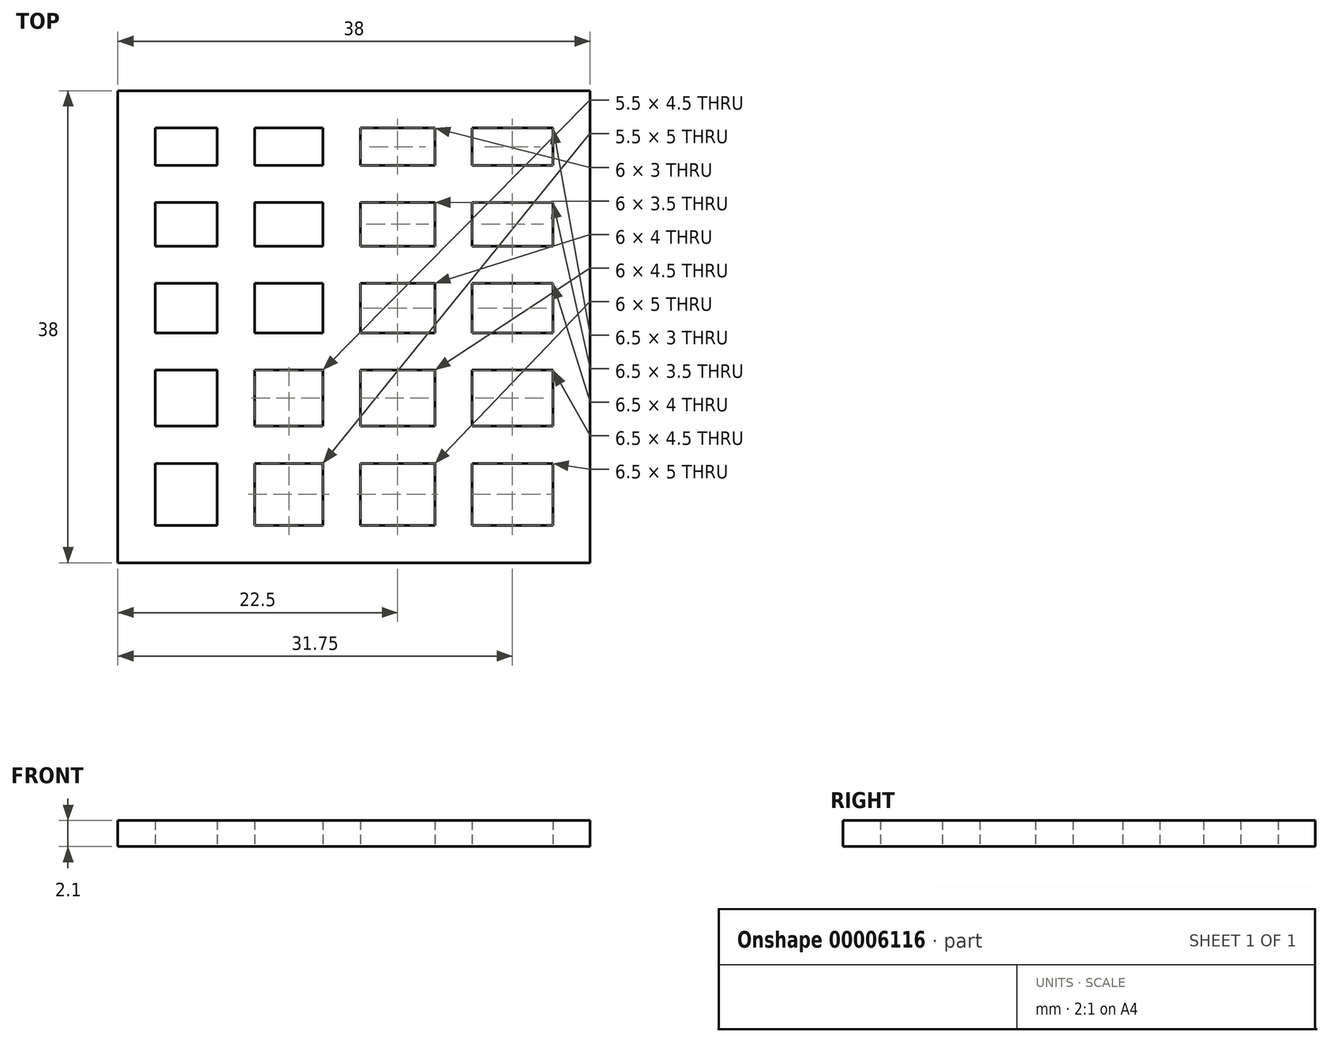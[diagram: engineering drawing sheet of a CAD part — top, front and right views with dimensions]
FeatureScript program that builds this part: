
annotation { "Feature Type Name" : "Feature", "Feature Type Description" : "" }
export const myFeature = defineFeature(function(context is Context, id is Id, definition is map)
    precondition{}
    {
        {
            var Q0;
            Q0=qCreatedBy(makeId("Top.planeOp"),FACE);
            var sketch = newSketch(context, id + "F0", { "sketchPlane" : qUnion([Q0])});
            skLineSegment(sketch, "E0.rect.bottom", {"start": v(8, -6) * mm, "end": v(3, -6) * mm});
            skLineSegment(sketch, "E0.rect.top", {"start": v(8, -3) * mm, "end": v(3, -3) * mm});
            skLineSegment(sketch, "E0.rect.left", {"start": v(8, -6) * mm, "end": v(8, -3) * mm});
            skLineSegment(sketch, "E0.rect.right", {"start": v(3, -6) * mm, "end": v(3, -3) * mm});
            skPoint(sketch, "E0.rect.middle", {"position": v(5.5, -4.5) * mm});
            skLineSegment(sketch, "E1.rect.bottom", {"start": v(8, -12.5) * mm, "end": v(3, -12.5) * mm});
            skLineSegment(sketch, "E1.rect.top", {"start": v(8, -9) * mm, "end": v(3, -9) * mm});
            skLineSegment(sketch, "E1.rect.left", {"start": v(8, -12.5) * mm, "end": v(8, -9) * mm});
            skLineSegment(sketch, "E1.rect.right", {"start": v(3, -12.5) * mm, "end": v(3, -9) * mm});
            skPoint(sketch, "E1.rect.middle", {"position": v(5.5, -10.75) * mm});
            skLineSegment(sketch, "E2.rect.bottom", {"start": v(8, -19.5) * mm, "end": v(3, -19.5) * mm});
            skLineSegment(sketch, "E2.rect.top", {"start": v(8, -15.5) * mm, "end": v(3, -15.5) * mm});
            skLineSegment(sketch, "E2.rect.left", {"start": v(8, -19.5) * mm, "end": v(8, -15.5) * mm});
            skLineSegment(sketch, "E2.rect.right", {"start": v(3, -19.5) * mm, "end": v(3, -15.5) * mm});
            skPoint(sketch, "E2.rect.middle", {"position": v(5.5, -17.5) * mm});
            skLineSegment(sketch, "E3.rect.bottom", {"start": v(8, -27) * mm, "end": v(3, -27) * mm});
            skLineSegment(sketch, "E3.rect.top", {"start": v(8, -22.5) * mm, "end": v(3, -22.5) * mm});
            skLineSegment(sketch, "E3.rect.left", {"start": v(8, -27) * mm, "end": v(8, -22.5) * mm});
            skLineSegment(sketch, "E3.rect.right", {"start": v(3, -27) * mm, "end": v(3, -22.5) * mm});
            skPoint(sketch, "E3.rect.middle", {"position": v(5.5, -24.75) * mm});
            skLineSegment(sketch, "E4.rect.bottom", {"start": v(8, -35) * mm, "end": v(3, -35) * mm});
            skLineSegment(sketch, "E4.rect.top", {"start": v(8, -30) * mm, "end": v(3, -30) * mm});
            skLineSegment(sketch, "E4.rect.left", {"start": v(8, -35) * mm, "end": v(8, -30) * mm});
            skLineSegment(sketch, "E4.rect.right", {"start": v(3, -35) * mm, "end": v(3, -30) * mm});
            skPoint(sketch, "E4.rect.middle", {"position": v(5.5, -32.5) * mm});
            skLineSegment(sketch, "E5.rect.bottom", {"start": v(16.5, -6) * mm, "end": v(11, -6) * mm});
            skLineSegment(sketch, "E5.rect.top", {"start": v(16.5, -3) * mm, "end": v(11, -3) * mm});
            skLineSegment(sketch, "E5.rect.left", {"start": v(16.5, -6) * mm, "end": v(16.5, -3) * mm});
            skLineSegment(sketch, "E5.rect.right", {"start": v(11, -6) * mm, "end": v(11, -3) * mm});
            skPoint(sketch, "E5.rect.middle", {"position": v(13.75, -4.5) * mm});
            skLineSegment(sketch, "E6.rect.bottom", {"start": v(16.5, -12.5) * mm, "end": v(11, -12.5) * mm});
            skLineSegment(sketch, "E6.rect.top", {"start": v(16.5, -9) * mm, "end": v(11, -9) * mm});
            skLineSegment(sketch, "E6.rect.left", {"start": v(16.5, -12.5) * mm, "end": v(16.5, -9) * mm});
            skLineSegment(sketch, "E6.rect.right", {"start": v(11, -12.5) * mm, "end": v(11, -9) * mm});
            skPoint(sketch, "E6.rect.middle", {"position": v(13.75, -10.75) * mm});
            skLineSegment(sketch, "E7.rect.bottom", {"start": v(16.5, -19.5) * mm, "end": v(11, -19.5) * mm});
            skLineSegment(sketch, "E7.rect.top", {"start": v(16.5, -15.5) * mm, "end": v(11, -15.5) * mm});
            skLineSegment(sketch, "E7.rect.left", {"start": v(16.5, -19.5) * mm, "end": v(16.5, -15.5) * mm});
            skLineSegment(sketch, "E7.rect.right", {"start": v(11, -19.5) * mm, "end": v(11, -15.5) * mm});
            skPoint(sketch, "E7.rect.middle", {"position": v(13.75, -17.5) * mm});
            skLineSegment(sketch, "E8.rect.bottom", {"start": v(16.5, -27) * mm, "end": v(11, -27) * mm});
            skLineSegment(sketch, "E8.rect.top", {"start": v(16.5, -22.5) * mm, "end": v(11, -22.5) * mm});
            skLineSegment(sketch, "E8.rect.left", {"start": v(16.5, -27) * mm, "end": v(16.5, -22.5) * mm});
            skLineSegment(sketch, "E8.rect.right", {"start": v(11, -27) * mm, "end": v(11, -22.5) * mm});
            skPoint(sketch, "E8.rect.middle", {"position": v(13.75, -24.75) * mm});
            skLineSegment(sketch, "E9.rect.bottom", {"start": v(16.5, -35) * mm, "end": v(11, -35) * mm});
            skLineSegment(sketch, "E9.rect.top", {"start": v(16.5, -30) * mm, "end": v(11, -30) * mm});
            skLineSegment(sketch, "E9.rect.left", {"start": v(16.5, -35) * mm, "end": v(16.5, -30) * mm});
            skLineSegment(sketch, "E9.rect.right", {"start": v(11, -35) * mm, "end": v(11, -30) * mm});
            skPoint(sketch, "E9.rect.middle", {"position": v(13.75, -32.5) * mm});
            skLineSegment(sketch, "E10.rect.bottom", {"start": v(25.5, -6) * mm, "end": v(19.5, -6) * mm});
            skLineSegment(sketch, "E10.rect.top", {"start": v(25.5, -3) * mm, "end": v(19.5, -3) * mm});
            skLineSegment(sketch, "E10.rect.left", {"start": v(25.5, -6) * mm, "end": v(25.5, -3) * mm});
            skLineSegment(sketch, "E10.rect.right", {"start": v(19.5, -6) * mm, "end": v(19.5, -3) * mm});
            skPoint(sketch, "E10.rect.middle", {"position": v(22.5, -4.5) * mm});
            skLineSegment(sketch, "E11.rect.bottom", {"start": v(25.5, -12.5) * mm, "end": v(19.5, -12.5) * mm});
            skLineSegment(sketch, "E11.rect.top", {"start": v(25.5, -9) * mm, "end": v(19.5, -9) * mm});
            skLineSegment(sketch, "E11.rect.left", {"start": v(25.5, -12.5) * mm, "end": v(25.5, -9) * mm});
            skLineSegment(sketch, "E11.rect.right", {"start": v(19.5, -12.5) * mm, "end": v(19.5, -9) * mm});
            skPoint(sketch, "E11.rect.middle", {"position": v(22.5, -10.75) * mm});
            skLineSegment(sketch, "E12.rect.bottom", {"start": v(25.5, -19.5) * mm, "end": v(19.5, -19.5) * mm});
            skLineSegment(sketch, "E12.rect.top", {"start": v(25.5, -15.5) * mm, "end": v(19.5, -15.5) * mm});
            skLineSegment(sketch, "E12.rect.left", {"start": v(25.5, -19.5) * mm, "end": v(25.5, -15.5) * mm});
            skLineSegment(sketch, "E12.rect.right", {"start": v(19.5, -19.5) * mm, "end": v(19.5, -15.5) * mm});
            skPoint(sketch, "E12.rect.middle", {"position": v(22.5, -17.5) * mm});
            skLineSegment(sketch, "E13.rect.bottom", {"start": v(25.5, -27) * mm, "end": v(19.5, -27) * mm});
            skLineSegment(sketch, "E13.rect.top", {"start": v(25.5, -22.5) * mm, "end": v(19.5, -22.5) * mm});
            skLineSegment(sketch, "E13.rect.left", {"start": v(25.5, -27) * mm, "end": v(25.5, -22.5) * mm});
            skLineSegment(sketch, "E13.rect.right", {"start": v(19.5, -27) * mm, "end": v(19.5, -22.5) * mm});
            skPoint(sketch, "E13.rect.middle", {"position": v(22.5, -24.75) * mm});
            skLineSegment(sketch, "E14.rect.bottom", {"start": v(25.5, -35) * mm, "end": v(19.5, -35) * mm});
            skLineSegment(sketch, "E14.rect.top", {"start": v(25.5, -30) * mm, "end": v(19.5, -30) * mm});
            skLineSegment(sketch, "E14.rect.left", {"start": v(25.5, -35) * mm, "end": v(25.5, -30) * mm});
            skLineSegment(sketch, "E14.rect.right", {"start": v(19.5, -35) * mm, "end": v(19.5, -30) * mm});
            skPoint(sketch, "E14.rect.middle", {"position": v(22.5, -32.5) * mm});
            skLineSegment(sketch, "E15.rect.bottom", {"start": v(35, -6) * mm, "end": v(28.5, -6) * mm});
            skLineSegment(sketch, "E15.rect.top", {"start": v(35, -3) * mm, "end": v(28.5, -3) * mm});
            skLineSegment(sketch, "E15.rect.left", {"start": v(35, -6) * mm, "end": v(35, -3) * mm});
            skLineSegment(sketch, "E15.rect.right", {"start": v(28.5, -6) * mm, "end": v(28.5, -3) * mm});
            skPoint(sketch, "E15.rect.middle", {"position": v(31.75, -4.5) * mm});
            skLineSegment(sketch, "E16.rect.bottom", {"start": v(35, -12.5) * mm, "end": v(28.5, -12.5) * mm});
            skLineSegment(sketch, "E16.rect.top", {"start": v(35, -9) * mm, "end": v(28.5, -9) * mm});
            skLineSegment(sketch, "E16.rect.left", {"start": v(35, -12.5) * mm, "end": v(35, -9) * mm});
            skLineSegment(sketch, "E16.rect.right", {"start": v(28.5, -12.5) * mm, "end": v(28.5, -9) * mm});
            skPoint(sketch, "E16.rect.middle", {"position": v(31.75, -10.75) * mm});
            skLineSegment(sketch, "E17.rect.bottom", {"start": v(35, -19.5) * mm, "end": v(28.5, -19.5) * mm});
            skLineSegment(sketch, "E17.rect.top", {"start": v(35, -15.5) * mm, "end": v(28.5, -15.5) * mm});
            skLineSegment(sketch, "E17.rect.left", {"start": v(35, -19.5) * mm, "end": v(35, -15.5) * mm});
            skLineSegment(sketch, "E17.rect.right", {"start": v(28.5, -19.5) * mm, "end": v(28.5, -15.5) * mm});
            skPoint(sketch, "E17.rect.middle", {"position": v(31.75, -17.5) * mm});
            skLineSegment(sketch, "E18.rect.bottom", {"start": v(35, -27) * mm, "end": v(28.5, -27) * mm});
            skLineSegment(sketch, "E18.rect.top", {"start": v(35, -22.5) * mm, "end": v(28.5, -22.5) * mm});
            skLineSegment(sketch, "E18.rect.left", {"start": v(35, -27) * mm, "end": v(35, -22.5) * mm});
            skLineSegment(sketch, "E18.rect.right", {"start": v(28.5, -27) * mm, "end": v(28.5, -22.5) * mm});
            skPoint(sketch, "E18.rect.middle", {"position": v(31.75, -24.75) * mm});
            skLineSegment(sketch, "E19.rect.bottom", {"start": v(35, -35) * mm, "end": v(28.5, -35) * mm});
            skLineSegment(sketch, "E19.rect.top", {"start": v(35, -30) * mm, "end": v(28.5, -30) * mm});
            skLineSegment(sketch, "E19.rect.left", {"start": v(35, -35) * mm, "end": v(35, -30) * mm});
            skLineSegment(sketch, "E19.rect.right", {"start": v(28.5, -35) * mm, "end": v(28.5, -30) * mm});
            skPoint(sketch, "E19.rect.middle", {"position": v(31.75, -32.5) * mm});
            skLineSegment(sketch, "E20.rect.bottom", {"start": v(38, -38) * mm, "end": v(0, -38) * mm});
            skLineSegment(sketch, "E20.rect.top", {"start": v(38, 0) * mm, "end": v(0, 0) * mm});
            skLineSegment(sketch, "E20.rect.left", {"start": v(38, -38) * mm, "end": v(38, 0) * mm});
            skLineSegment(sketch, "E20.rect.right", {"start": v(0, -38) * mm, "end": v(0, 0) * mm});
            skPoint(sketch, "E20.rect.middle", {"position": v(0, 0) * mm});
            skSolve(sketch);
        }
        {
            var Q0;
            Q0=makeQuery(id+"F0.imprint","IMPRINT",FACE,{"disambiguationData":[TD([[makeQuery(id+"F0.imprint","IMPRINT",EDGE,{"derivedFrom":sQuery(id+"F0.wireOp",EDGE,"E0.rect.bottom")}),1.0]])]});
            extrude(context, id + "F1", {"entities" : qUnion([Q0]), "depth" : 2.1 * mm});
        }
    });
